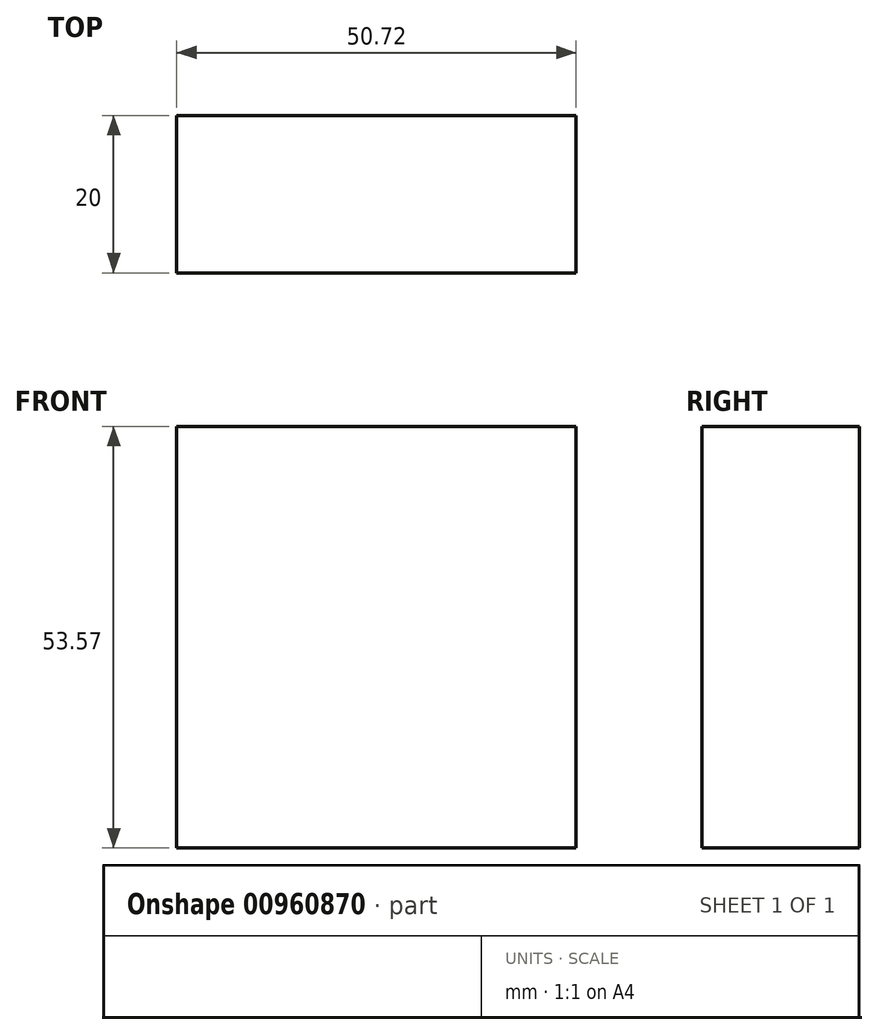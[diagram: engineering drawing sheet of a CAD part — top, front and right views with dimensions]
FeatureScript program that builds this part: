
annotation { "Feature Type Name" : "Feature", "Feature Type Description" : "" }
export const myFeature = defineFeature(function(context is Context, id is Id, definition is map)
    precondition{}
    {
        {
            var Q0;
            Q0=qCreatedBy(makeId("Front.planeOp"),FACE);
            var sketch = newSketch(context, id + "F0", { "sketchPlane" : qUnion([Q0])});
            skLineSegment(sketch, "E0", {"start": v(0, 0) * mm, "end": v(0, 53.57) * mm});
            skLineSegment(sketch, "E1", {"start": v(0, 53.57) * mm, "end": v(-50.72, 53.57) * mm});
            skLineSegment(sketch, "E2", {"start": v(-50.72, 53.57) * mm, "end": v(-50.72, 0) * mm});
            skLineSegment(sketch, "E3", {"start": v(-50.72, 0) * mm, "end": v(0, 0) * mm});
            skSolve(sketch);
        }
        {
            var Q0;
            Q0 = qSketchRegion(id + "F0", true);
            extrude(context, id + "F1", {"entities" : qUnion([Q0]), "depth" : 20 * mm, "offsetDistance" : 25.4 * mm});
        }
    });
